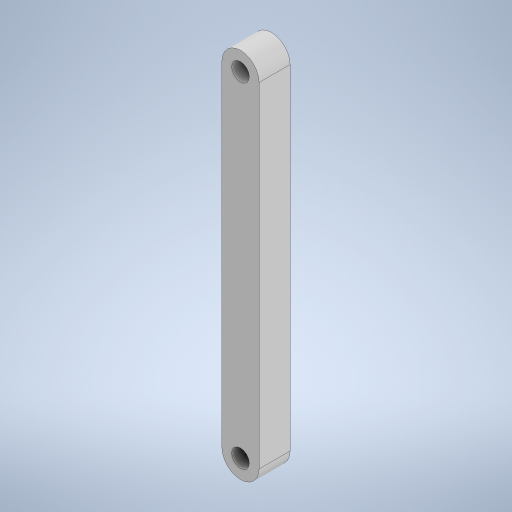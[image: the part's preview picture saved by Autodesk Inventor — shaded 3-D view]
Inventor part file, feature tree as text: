
AUTODESK INVENTOR PART (.ipt)
format: ipt  version: 2023 (Build 270158000, 158)  size: 242,176 bytes
history: native  units: mm
features: extrude x1, sketch x1
ambient origin geometry x8: Origin, YZ Plane, XZ Plane, XY Plane, X Axis, Y Axis, Z Axis, Center Point
bodies: Solid1 (feature_tree)
feature tree (2):
  extrude  "Extrusion1"  Depth=6.0mm
  sketch  "Sketch1"  dims[d8=5.0mm d9=0.0mm d10=6.0mm d11=60.0mm d12=3.0mm d13=6.0mm d14=2.85mm d15=3.0mm d16=6.0mm d17=2.85mm]
